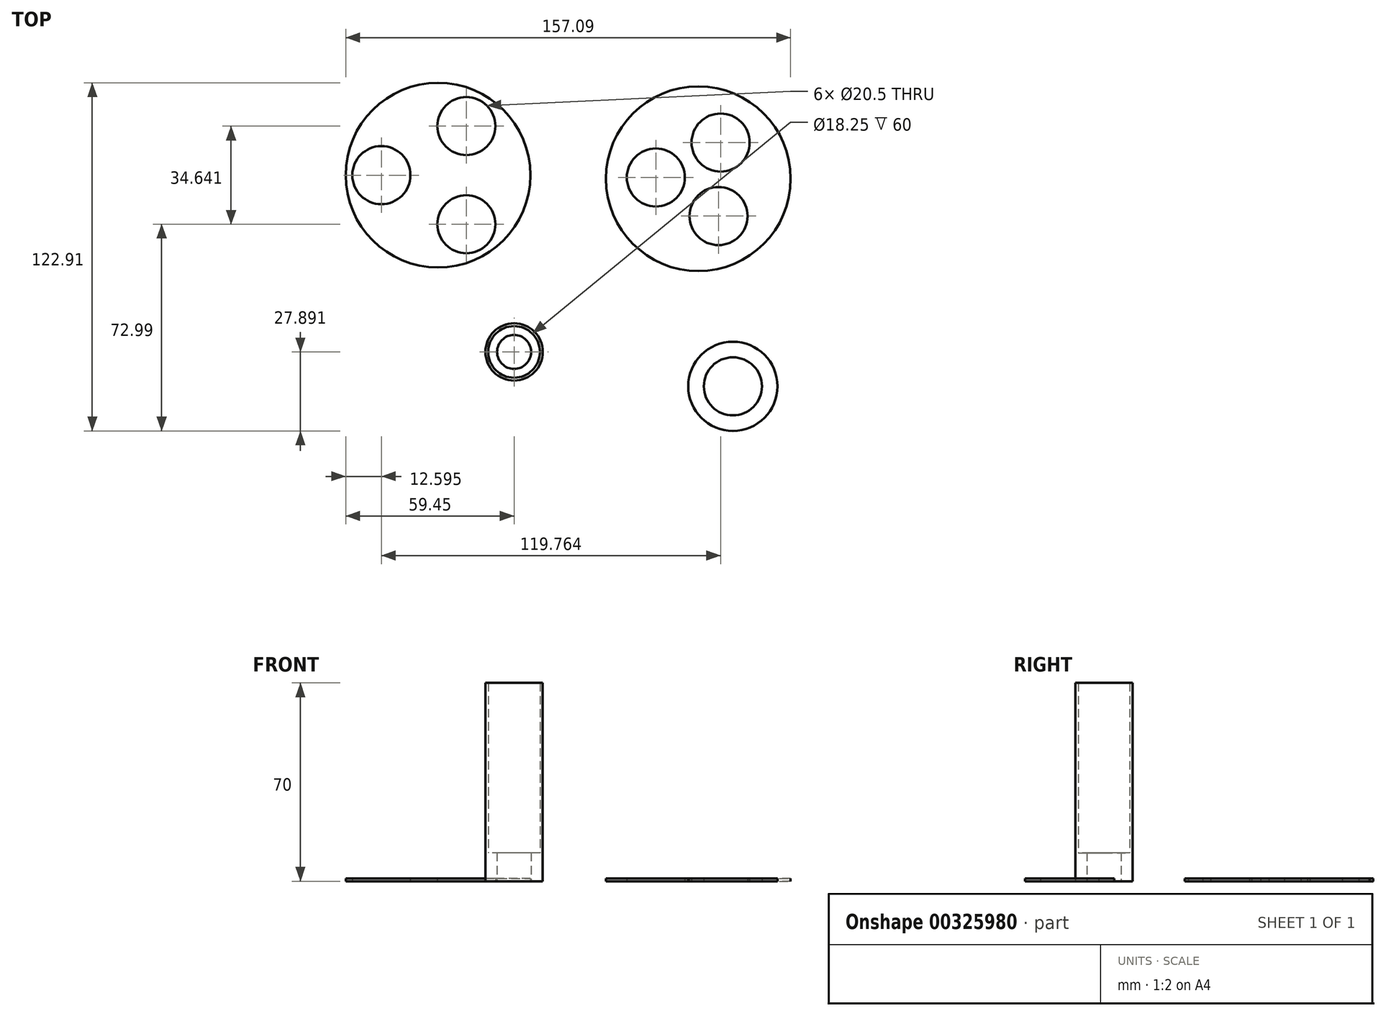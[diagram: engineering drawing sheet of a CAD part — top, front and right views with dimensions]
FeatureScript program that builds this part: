
annotation { "Feature Type Name" : "Feature", "Feature Type Description" : "" }
export const myFeature = defineFeature(function(context is Context, id is Id, definition is map)
    precondition{}
    {
        {
            var Q0;
            Q0=qCreatedBy(makeId("Top.planeOp"),FACE);
            var sketch = newSketch(context, id + "F0", { "sketchPlane" : qUnion([Q0])});
            skCircle(sketch, "E0", {"center": v(-64.32, 40.01) * mm, "radius": 32.6 * mm});
            skCircle(sketch, "E1", {"center": v(-37.47, -22.4) * mm, "radius": 9.12 * mm});
            skCircle(sketch, "E2", {"center": v(-37.47, -22.4) * mm, "radius": 6 * mm});
            skCircle(sketch, "E3", {"center": v(-84.32, 40.01) * mm, "radius": 10.25 * mm});
            skCircle(sketch, "E4.1.0", {"center": v(-54.32, 22.69) * mm, "radius": 10.25 * mm});
            skCircle(sketch, "E4.2.0", {"center": v(-54.32, 57.33) * mm, "radius": 10.25 * mm});
            skCircle(sketch, "E5", {"center": v(27.57, 38.76) * mm, "radius": 32.6 * mm});
            skCircle(sketch, "E6", {"center": v(12.58, 39.19) * mm, "radius": 10.25 * mm});
            skCircle(sketch, "E7.1.0", {"center": v(34.7, 25.56) * mm, "radius": 10.25 * mm});
            skCircle(sketch, "E7.2.0", {"center": v(35.44, 51.53) * mm, "radius": 10.25 * mm});
            skCircle(sketch, "E8", {"center": v(-37.47, -22.4) * mm, "radius": 10.12 * mm});
            skCircle(sketch, "E9", {"center": v(39.77, -34.55) * mm, "radius": 15.75 * mm});
            skCircle(sketch, "E10", {"center": v(39.77, -34.55) * mm, "radius": 10.25 * mm});
            skSolve(sketch);
        }
        {
            var Q0;
            Q0=makeQuery(id+"F0.imprint","IMPRINT",FACE,{"disambiguationData":[TD([[makeQuery(id+"F0.imprint","IMPRINT",EDGE,{"derivedFrom":sQuery(id+"F0.wireOp",EDGE,"E0")}),1.0]])]});
            var Q1;
            Q1=makeQuery(id+"F0.imprint","IMPRINT",FACE,{"disambiguationData":[TD([[makeQuery(id+"F0.imprint","IMPRINT",EDGE,{"derivedFrom":sQuery(id+"F0.wireOp",EDGE,"E5")}),1.0]])]});
            extrude(context, id + "F1", {"entities" : qUnion([Q0, Q1]), "depth" : 1 * mm, "offsetDistance" : 25 * mm});
        }
        {
            var Q0;
            Q0=makeQuery(id+"F0.imprint","IMPRINT",FACE,{"disambiguationData":[TD([[makeQuery(id+"F0.imprint","IMPRINT",EDGE,{"derivedFrom":sQuery(id+"F0.wireOp",EDGE,"E1")}),-1.0]])]});
            extrude(context, id + "F2", {"entities" : qUnion([Q0]), "depth" : 70 * mm, "offsetDistance" : 25 * mm});
        }
        {
            var Q0;
            Q0=makeQuery(id+"F0.imprint","IMPRINT",FACE,{"disambiguationData":[TD([[makeQuery(id+"F0.imprint","IMPRINT",EDGE,{"derivedFrom":sQuery(id+"F0.wireOp",EDGE,"E1")}),1.0]])]});
            extrude(context, id + "F3", {"entities" : qUnion([Q0]), "operationType" : NewBodyOperationType.ADD, "depth" : 10 * mm, "offsetDistance" : 25 * mm});
        }
        {
            var Q0;
            Q0=makeQuery(id+"F0.imprint","IMPRINT",FACE,{"disambiguationData":[TD([[makeQuery(id+"F0.imprint","IMPRINT",EDGE,{"derivedFrom":sQuery(id+"F0.wireOp",EDGE,"E9")}),1.0]])]});
            extrude(context, id + "F4", {"entities" : qUnion([Q0]), "depth" : 1 * mm, "offsetDistance" : 25 * mm});
        }
    });
